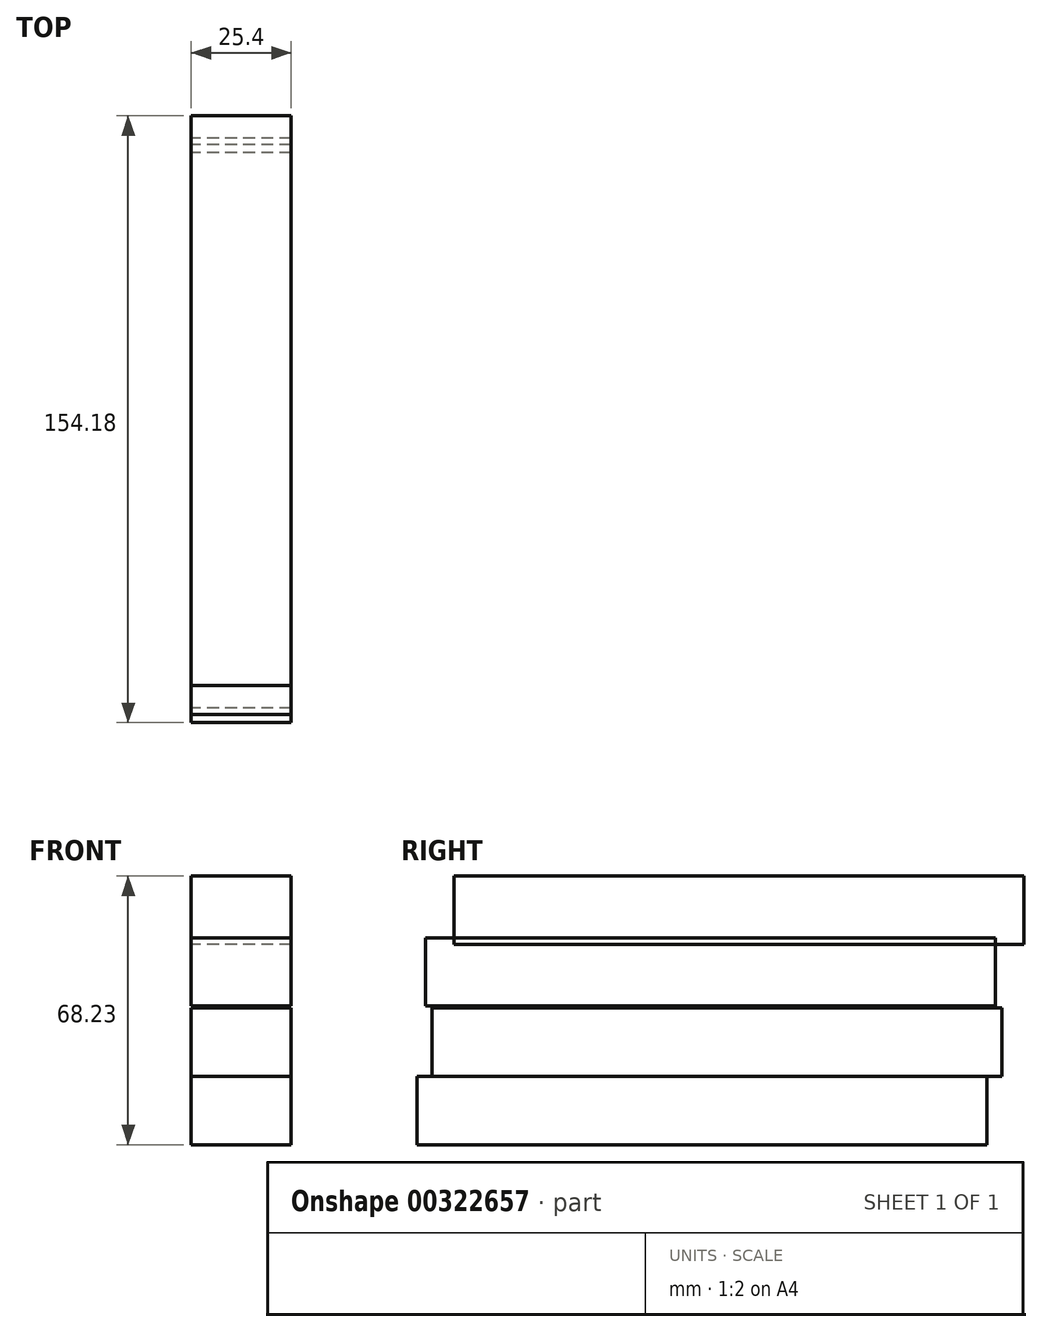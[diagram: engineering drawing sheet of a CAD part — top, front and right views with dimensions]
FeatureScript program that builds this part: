
annotation { "Feature Type Name" : "Feature", "Feature Type Description" : "" }
export const myFeature = defineFeature(function(context is Context, id is Id, definition is map)
    precondition{}
    {
        {
            var Q0;
            Q0=qCreatedBy(makeId("Right.planeOp"),FACE);
            var sketch = newSketch(context, id + "F0", { "sketchPlane" : qUnion([Q0])});
            skLineSegment(sketch, "E0.bottom", {"start": v(88.38, -5.98) * mm, "end": v(-56.4, -5.98) * mm});
            skLineSegment(sketch, "E0.top", {"start": v(88.38, 11.38) * mm, "end": v(-56.4, 11.38) * mm});
            skLineSegment(sketch, "E0.left", {"start": v(88.38, -5.98) * mm, "end": v(88.38, 11.38) * mm});
            skLineSegment(sketch, "E0.right", {"start": v(-56.4, -5.98) * mm, "end": v(-56.4, 11.38) * mm});
            skLineSegment(sketch, "E1.bottom", {"start": v(92.1, 11.42) * mm, "end": v(-52.67, 11.42) * mm});
            skLineSegment(sketch, "E1.top", {"start": v(92.1, 28.79) * mm, "end": v(-52.67, 28.79) * mm});
            skLineSegment(sketch, "E1.left", {"start": v(92.1, 11.42) * mm, "end": v(92.1, 28.79) * mm});
            skLineSegment(sketch, "E1.right", {"start": v(-52.67, 11.42) * mm, "end": v(-52.67, 28.79) * mm});
            skLineSegment(sketch, "E2.bottom", {"start": v(90.49, 29.23) * mm, "end": v(-54.28, 29.23) * mm});
            skLineSegment(sketch, "E2.top", {"start": v(90.49, 46.6) * mm, "end": v(-54.28, 46.6) * mm});
            skLineSegment(sketch, "E2.left", {"start": v(90.49, 29.23) * mm, "end": v(90.49, 46.6) * mm});
            skLineSegment(sketch, "E2.right", {"start": v(-54.28, 29.23) * mm, "end": v(-54.28, 46.6) * mm});
            skLineSegment(sketch, "E3.bottom", {"start": v(97.78, 44.88) * mm, "end": v(-47, 44.88) * mm});
            skLineSegment(sketch, "E3.top", {"start": v(97.78, 62.25) * mm, "end": v(-47, 62.25) * mm});
            skLineSegment(sketch, "E3.left", {"start": v(97.78, 44.88) * mm, "end": v(97.78, 62.25) * mm});
            skLineSegment(sketch, "E3.right", {"start": v(-47, 44.88) * mm, "end": v(-47, 62.25) * mm});
            skSolve(sketch);
        }
        {
            var Q0;
            Q0=qCreatedBy(makeId("Right.planeOp"),FACE);
            var sketch = newSketch(context, id + "F1", { "sketchPlane" : qUnion([Q0])});
            skSolve(sketch);
        }
        {
            var Q0;
            Q0 = qSketchRegion(id + "F1", true);
            var Q1;
            Q1=makeQuery(id+"F0.imprint","IMPRINT",FACE,{"disambiguationData":[TD([[makeQuery(id+"F0.imprint","IMPRINT",EDGE,{"derivedFrom":sQuery(id+"F0.wireOp",EDGE,"E0.bottom")}),-1.0]])]});
            extrude(context, id + "F2", {"entities" : qUnion([Q0, Q1]), "depth" : 25.4 * mm});
        }
        {
            var Q0;
            Q0=makeQuery(id+"F0.imprint","IMPRINT",FACE,{"disambiguationData":[TD([[makeQuery(id+"F0.imprint","IMPRINT",EDGE,{"derivedFrom":sQuery(id+"F0.wireOp",EDGE,"E1.bottom")}),-1.0]])]});
            var Q1;
            {var subQ1=sQuery(id+"F0.wireOp",EDGE,"E2.bottom");Q1=makeQuery(id+"F0.imprint","IMPRINT",FACE,{"disambiguationData":[TD([[makeQuery(id+"F0.imprint","IMPRINT",EDGE,{"derivedFrom":subQ1}),-1.0]])]});}
            var Q2;
            {var subQ0=sQuery(id+"F0.wireOp",EDGE,"E3.top");Q2=makeQuery(id+"F0.imprint","IMPRINT",FACE,{"disambiguationData":[TD([[makeQuery(id+"F0.imprint","IMPRINT",EDGE,{"derivedFrom":subQ0}),1.0]])]});}
            extrude(context, id + "F3", {"entities" : qUnion([Q0, Q1, Q2]), "depth" : 25.4 * mm});
        }
    });
